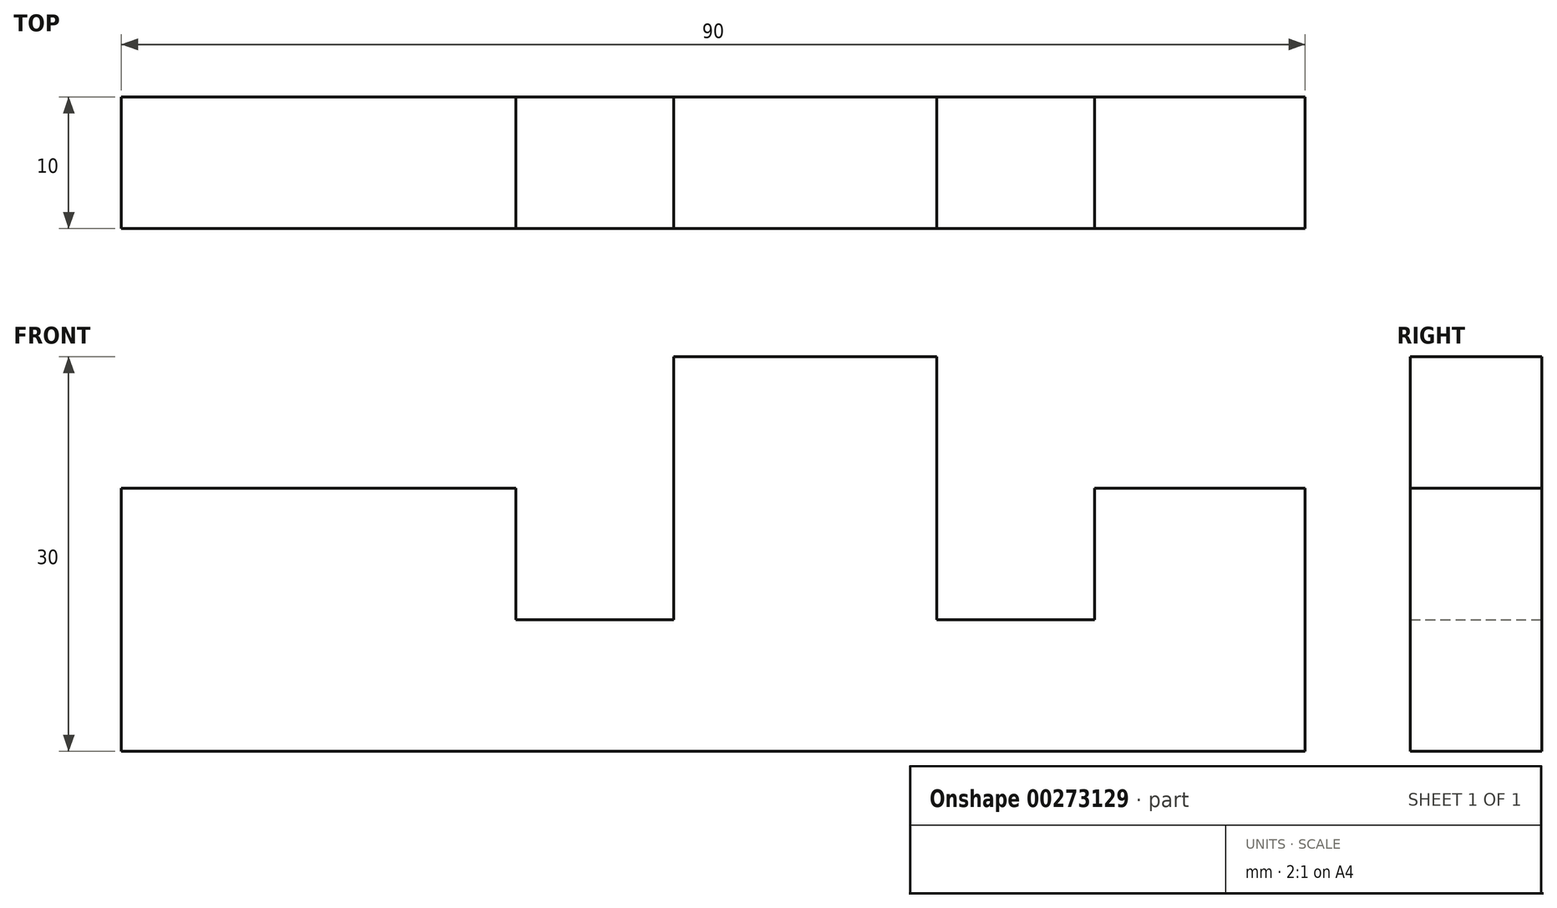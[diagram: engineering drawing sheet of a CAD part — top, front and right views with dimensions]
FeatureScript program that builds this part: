
annotation { "Feature Type Name" : "Feature", "Feature Type Description" : "" }
export const myFeature = defineFeature(function(context is Context, id is Id, definition is map)
    precondition{}
    {
        {
            var Q0;
            Q0=qCreatedBy(makeId("Front.planeOp"),FACE);
            var sketch = newSketch(context, id + "F0", { "sketchPlane" : qUnion([Q0])});
            skLineSegment(sketch, "E0", {"start": v(0, 0) * mm, "end": v(90, 0) * mm});
            skLineSegment(sketch, "E1", {"start": v(0, 0) * mm, "end": v(0, 20) * mm});
            skLineSegment(sketch, "E2", {"start": v(0, 20) * mm, "end": v(30, 20) * mm});
            skLineSegment(sketch, "E3", {"start": v(30, 20) * mm, "end": v(30, 10) * mm});
            skLineSegment(sketch, "E4", {"start": v(30, 10) * mm, "end": v(42, 10) * mm});
            skLineSegment(sketch, "E5", {"start": v(42, 10) * mm, "end": v(42, 30) * mm});
            skLineSegment(sketch, "E6", {"start": v(42, 30) * mm, "end": v(62, 30) * mm});
            skLineSegment(sketch, "E7", {"start": v(62, 30) * mm, "end": v(62, 10) * mm});
            skLineSegment(sketch, "E8", {"start": v(62, 10) * mm, "end": v(74, 10) * mm});
            skLineSegment(sketch, "E9", {"start": v(74, 10) * mm, "end": v(74, 20) * mm});
            skLineSegment(sketch, "E10", {"start": v(74, 20) * mm, "end": v(90, 20) * mm});
            skLineSegment(sketch, "E11", {"start": v(90, 0) * mm, "end": v(90, 20) * mm});
            skSolve(sketch);
        }
        {
            var Q0;
            Q0=makeQuery(id+"F0.imprint","IMPRINT",FACE,{"disambiguationData":[TD([[makeQuery(id+"F0.imprint","IMPRINT",EDGE,{"derivedFrom":sQuery(id+"F0.wireOp",EDGE,"E0")}),1.0]])]});
            extrude(context, id + "F1", {"entities" : qUnion([Q0]), "depth" : 10 * mm});
        }
    });
